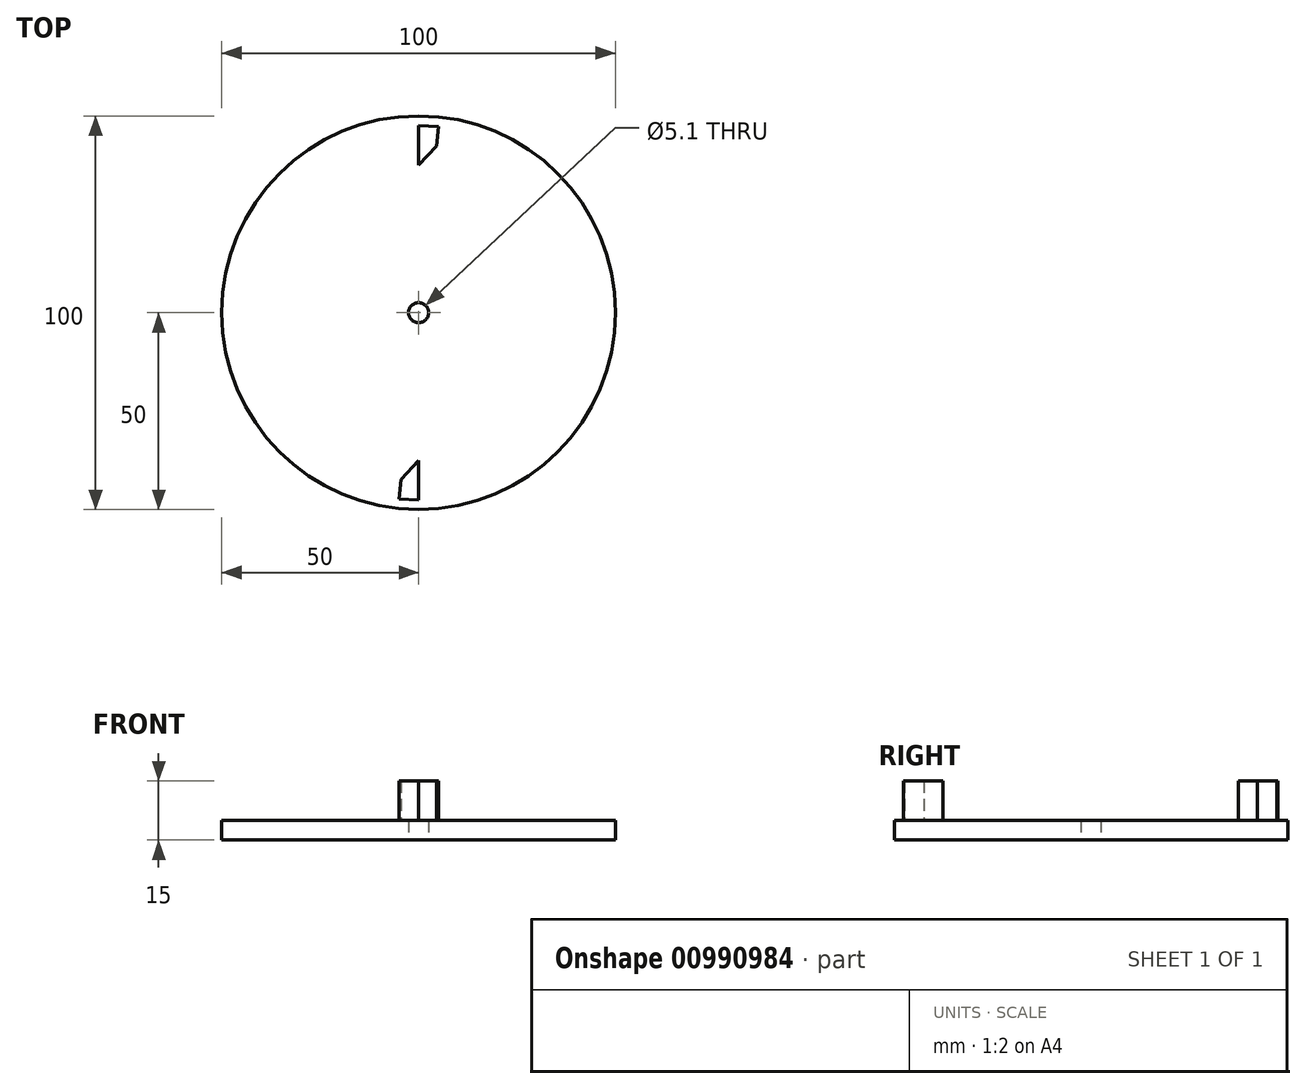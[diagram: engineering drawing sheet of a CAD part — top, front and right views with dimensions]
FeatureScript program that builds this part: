
annotation { "Feature Type Name" : "Feature", "Feature Type Description" : "" }
export const myFeature = defineFeature(function(context is Context, id is Id, definition is map)
    precondition{}
    {
        {
            var Q0;
            Q0=qCreatedBy(makeId("Top.planeOp"),FACE);
            var sketch = newSketch(context, id + "F0", { "sketchPlane" : qUnion([Q0])});
            skCircle(sketch, "E0", {"center": v(0, 0) * mm, "radius": 50 * mm});
            skCircle(sketch, "E1", {"center": v(0, 0) * mm, "radius": 2.55 * mm});
            skLineSegment(sketch, "E2", {"start": v(0, 49.94) * mm, "end": v(0, -49.94) * mm, "construction": true});
            skLineSegment(sketch, "E3", {"start": v(-15.61, -47.5) * mm, "end": v(15.61, -47.5) * mm, "construction": true});
            skCircle(sketch, "E4", {"center": v(0, 0) * mm, "radius": 47.5 * mm, "construction": true});
            skLineSegment(sketch, "E5", {"start": v(0, 0) * mm, "end": v(-5.26, -49.72) * mm, "construction": true});
            skSolve(sketch);
        }
        {
            var Q0;
            Q0 = qSketchRegion(id + "F0", true);
            extrude(context, id + "F1", {"entities" : qUnion([Q0]), "depth" : 5 * mm, "offsetDistance" : 25 * mm});
        }
        {
            var Q0;
            Q0=makeQuery(id+"F1.opExtrude","CAP_FACE",FACE,{"disambiguationData":[OSD([sQuery(id+"F0.wireOp",EDGE,"E0"),sQuery(id+"F0.wireOp",EDGE,"E1"),sQuery(id+"F0.wireOp",EDGE,"nrcRH9Lr-BUHX-WzhT-T5Kt-GjfWP7PtVsxk"),sQuery(id+"F0.wireOp",EDGE,"SAIIigb4-uInk-CD2I-8oU9-WajaqAXRIimh"),sQuery(id+"F0.wireOp",EDGE,"DxS7km8p-4tLx-IO32-nC6Z-gjxZCcnOAHh4"),sQuery(id+"F0.wireOp",EDGE,"X3iLT8yg-2PXE-DNtD-IR5C-jXUjXmiKGE2O"),sQuery(id+"F0.wireOp",EDGE,"f50f459c-82de-41c6-9814-dad84274bf13"),sQuery(id+"F0.wireOp",EDGE,"c1f580f5-98cc-4fd7-8b7c-4104b3eb98a7"),sQuery(id+"F0.wireOp",EDGE,"59ac1903-8a28-410f-9a9e-23b7377d0cfc"),sQuery(id+"F0.wireOp",EDGE,"c85b98ac-f18e-4bcc-a708-a0ba2dfc9529")])],"isStart":false});
            var sketch = newSketch(context, id + "F2", { "sketchPlane" : qUnion([Q0])});
            skLineSegment(sketch, "E6", {"start": v(0, -47.62) * mm, "end": v(0, -37.62) * mm});
            skLineSegment(sketch, "E7", {"start": v(0, -37.62) * mm, "end": v(-4.47, -42.39) * mm});
            skLineSegment(sketch, "E8", {"start": v(-4.47, -42.39) * mm, "end": v(-5, -47.36) * mm});
            skLineSegment(sketch, "E9", {"start": v(-5, -47.36) * mm, "end": v(0, -47.62) * mm});
            skLineSegment(sketch, "E10", {"start": v(0.05, 47.5) * mm, "end": v(0.05, 37.5) * mm});
            skLineSegment(sketch, "E11", {"start": v(0.05, 37.5) * mm, "end": v(4.52, 42.26) * mm});
            skLineSegment(sketch, "E12", {"start": v(4.52, 42.26) * mm, "end": v(5.05, 47.23) * mm});
            skLineSegment(sketch, "E13", {"start": v(5.05, 47.23) * mm, "end": v(0.05, 47.5) * mm});
            skLineSegment(sketch, "E14", {"start": v(0.05, 50) * mm, "end": v(0, -50) * mm, "construction": true});
            skSolve(sketch);
        }
        {
            var Q0;
            Q0=makeQuery(id+"F2.imprint","IMPRINT",FACE,{"disambiguationData":[TD([[makeQuery(id+"F2.imprint","IMPRINT",EDGE,{"derivedFrom":sQuery(id+"F2.wireOp",EDGE,"E10")}),1.0]])]});
            var Q1;
            Q1=makeQuery(id+"F2.imprint","IMPRINT",FACE,{"disambiguationData":[TD([[makeQuery(id+"F2.imprint","IMPRINT",EDGE,{"derivedFrom":sQuery(id+"F2.wireOp",EDGE,"E6")}),1.0]])]});
            extrude(context, id + "F3", {"entities" : qUnion([Q0, Q1]), "operationType" : NewBodyOperationType.ADD, "depth" : 10 * mm, "offsetDistance" : 25 * mm});
        }
    });
